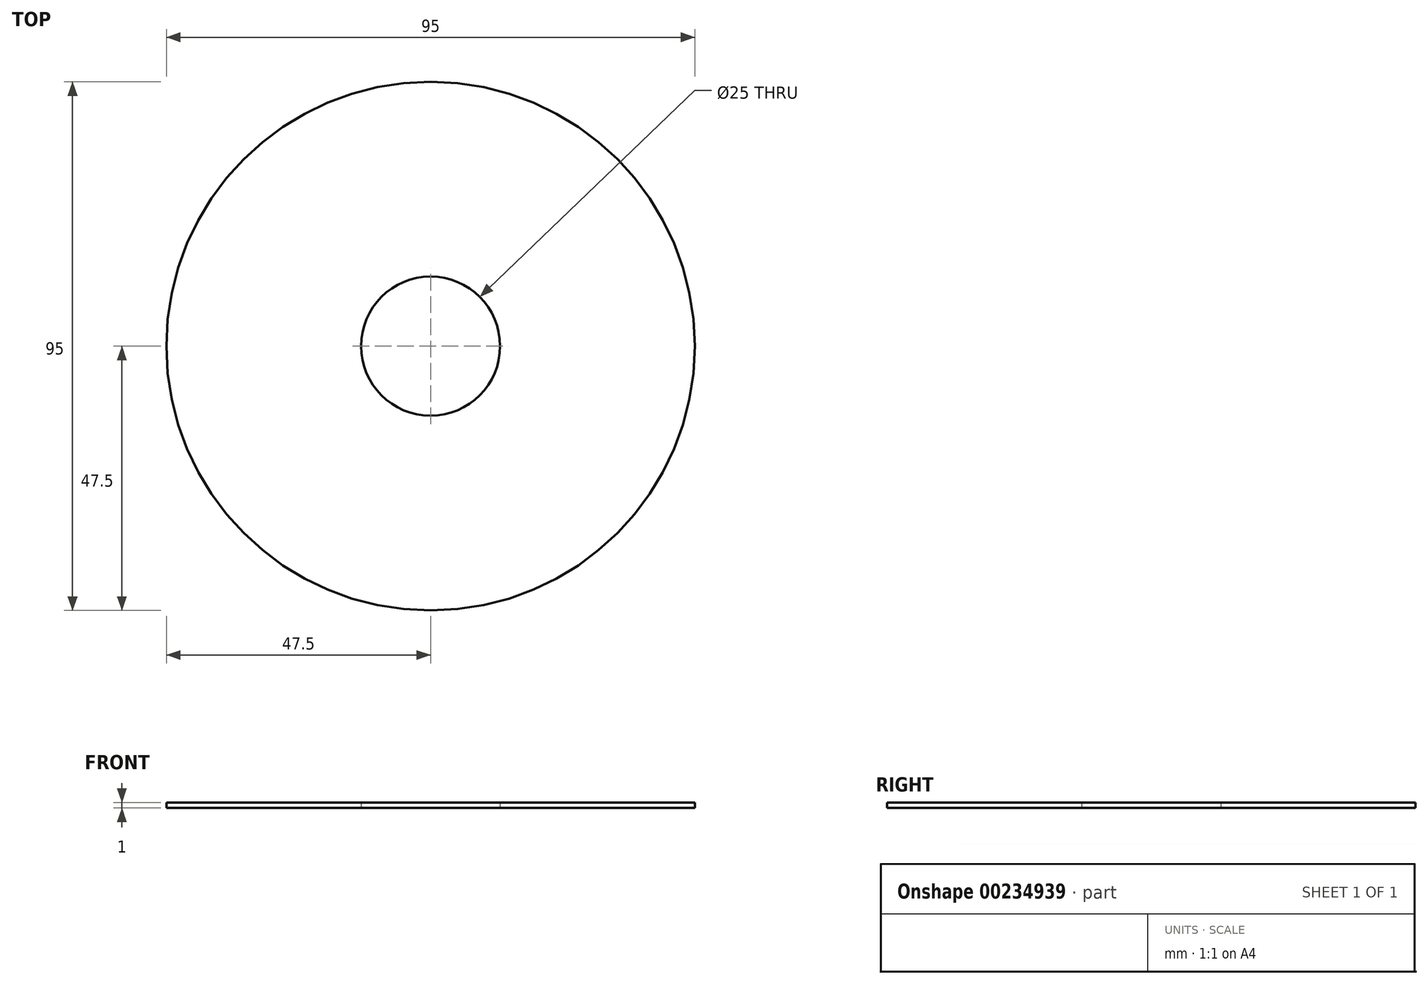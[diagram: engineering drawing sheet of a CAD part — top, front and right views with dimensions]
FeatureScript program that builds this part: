
annotation { "Feature Type Name" : "Feature", "Feature Type Description" : "" }
export const myFeature = defineFeature(function(context is Context, id is Id, definition is map)
    precondition{}
    {
        {
            var Q0;
            Q0=qCreatedBy(makeId("Top.planeOp"),FACE);
            var sketch = newSketch(context, id + "F0", { "sketchPlane" : qUnion([Q0])});
            skCircle(sketch, "E0", {"center": v(0, 0) * mm, "radius": 47.5 * mm});
            skCircle(sketch, "E1", {"center": v(0, 0) * mm, "radius": 12.5 * mm});
            skSolve(sketch);
        }
        {
            var Q0;
            Q0 = qSketchRegion(id + "F0", true);
            extrude(context, id + "F1", {"entities" : qUnion([Q0]), "depth" : 1 * mm});
        }
    });
